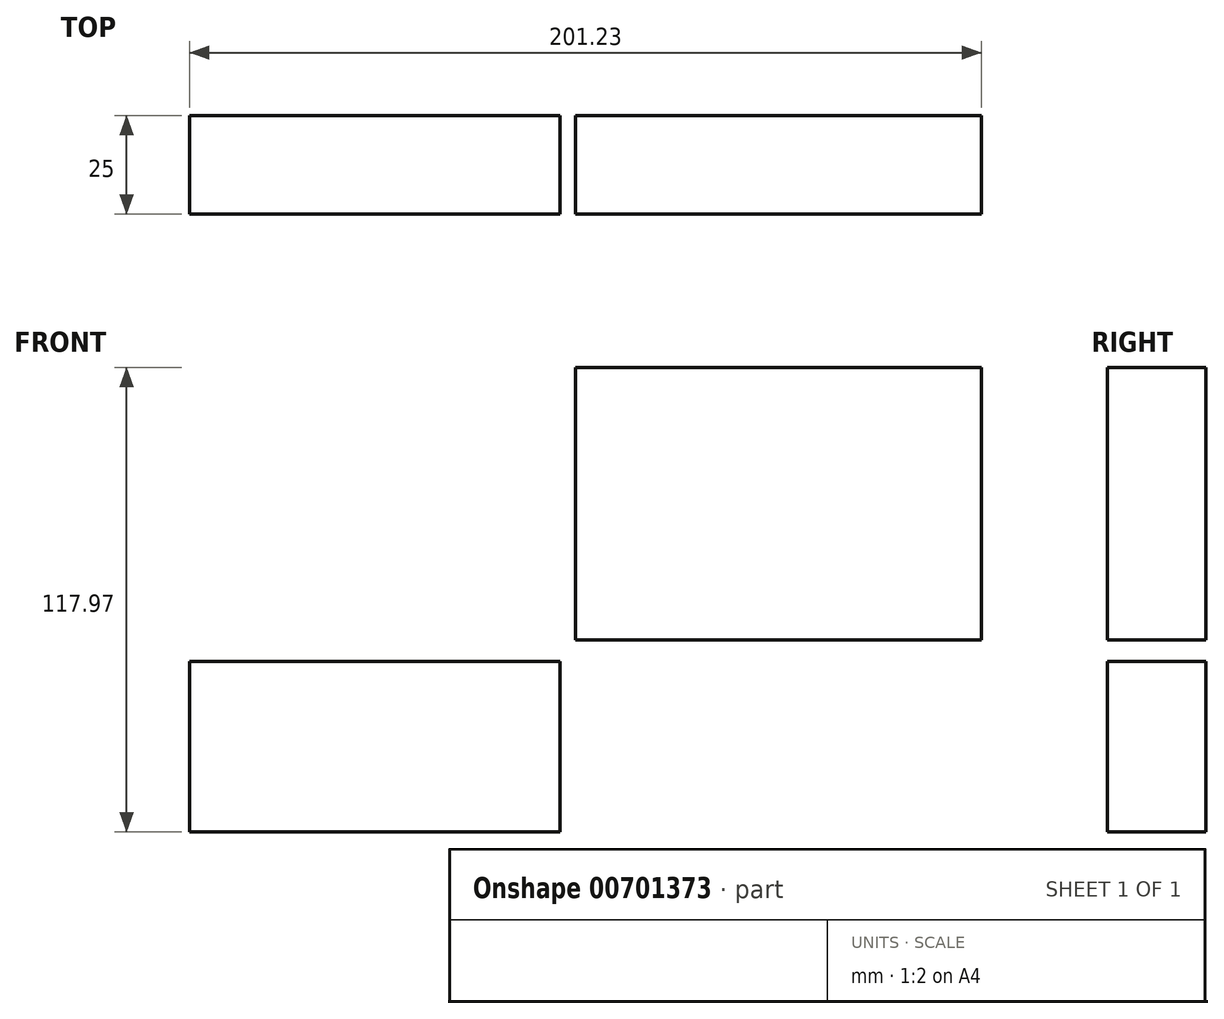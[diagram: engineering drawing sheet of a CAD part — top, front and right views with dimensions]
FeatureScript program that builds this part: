
annotation { "Feature Type Name" : "Feature", "Feature Type Description" : "" }
export const myFeature = defineFeature(function(context is Context, id is Id, definition is map)
    precondition{}
    {
        {
            var Q0;
            Q0=qCreatedBy(makeId("Front.planeOp"),FACE);
            var sketch = newSketch(context, id + "F0", { "sketchPlane" : qUnion([Q0])});
            skLineSegment(sketch, "E0.bottom", {"start": v(-194.25, 0) * mm, "end": v(-100.13, 0) * mm});
            skLineSegment(sketch, "E0.top", {"start": v(-194.25, -43.35) * mm, "end": v(-100.13, -43.35) * mm});
            skLineSegment(sketch, "E0.left", {"start": v(-194.25, 0) * mm, "end": v(-194.25, -43.35) * mm});
            skLineSegment(sketch, "E0.right", {"start": v(-100.13, 0) * mm, "end": v(-100.13, -43.35) * mm});
            skLineSegment(sketch, "E1.bottom", {"start": v(-96.23, 74.62) * mm, "end": v(6.98, 74.62) * mm});
            skLineSegment(sketch, "E1.top", {"start": v(-96.23, 5.42) * mm, "end": v(6.98, 5.42) * mm});
            skLineSegment(sketch, "E1.left", {"start": v(-96.23, 74.62) * mm, "end": v(-96.23, 5.42) * mm});
            skLineSegment(sketch, "E1.right", {"start": v(6.98, 74.62) * mm, "end": v(6.98, 5.42) * mm});
            skSolve(sketch);
        }
        {
            var Q0;
            Q0 = qSketchRegion(id + "F0", true);
            extrude(context, id + "F1", {"entities" : qUnion([Q0]), "depth" : 25 * mm, "offsetDistance" : 25 * mm});
        }
    });
